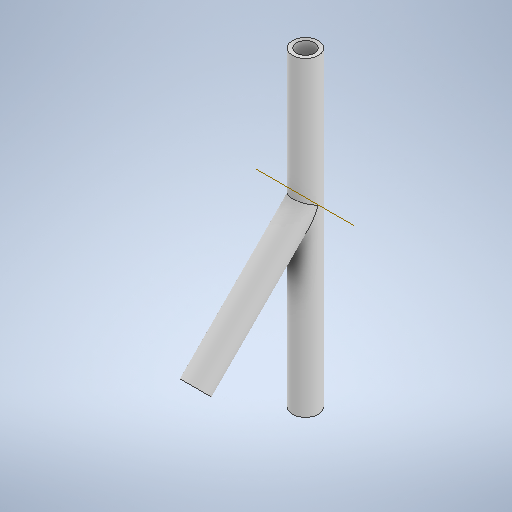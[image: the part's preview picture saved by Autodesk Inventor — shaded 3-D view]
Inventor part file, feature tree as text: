
AUTODESK INVENTOR PART (.ipt)
format: ipt  version: 2025 (Build 290162000, 162)  size: 276,480 bytes
history: native  units: mm
features: extrude x5, sketch x5, other x2
ambient origin geometry x8: Origin, YZ Plane, XZ Plane, XY Plane, X Axis, Y Axis, Z Axis, Center Point
bodies: Body1 (feature_tree)
feature tree (12):
  other  "Bryła1"
  other  "Płaszczyzna konstrukcyjna9"
  extrude  "Wyciągnięcie proste1"  Depth=10.0mm
  extrude  "Wyciągnięcie proste2"  Depth=60.0mm TaperAngle=0.0deg
  extrude  "Wyciągnięcie proste3"  Depth=10.0mm
  extrude  "Wyciągnięcie proste4"  Depth=140.0mm TaperAngle=0.0deg
  extrude  "Wyciągnięcie proste5"  Depth=7.0mm
  sketch  "Szkic5"
  sketch  "Szkic6"
  sketch  "Szkic8"
  sketch  "Szkic9"
  sketch  "Szkic10"
